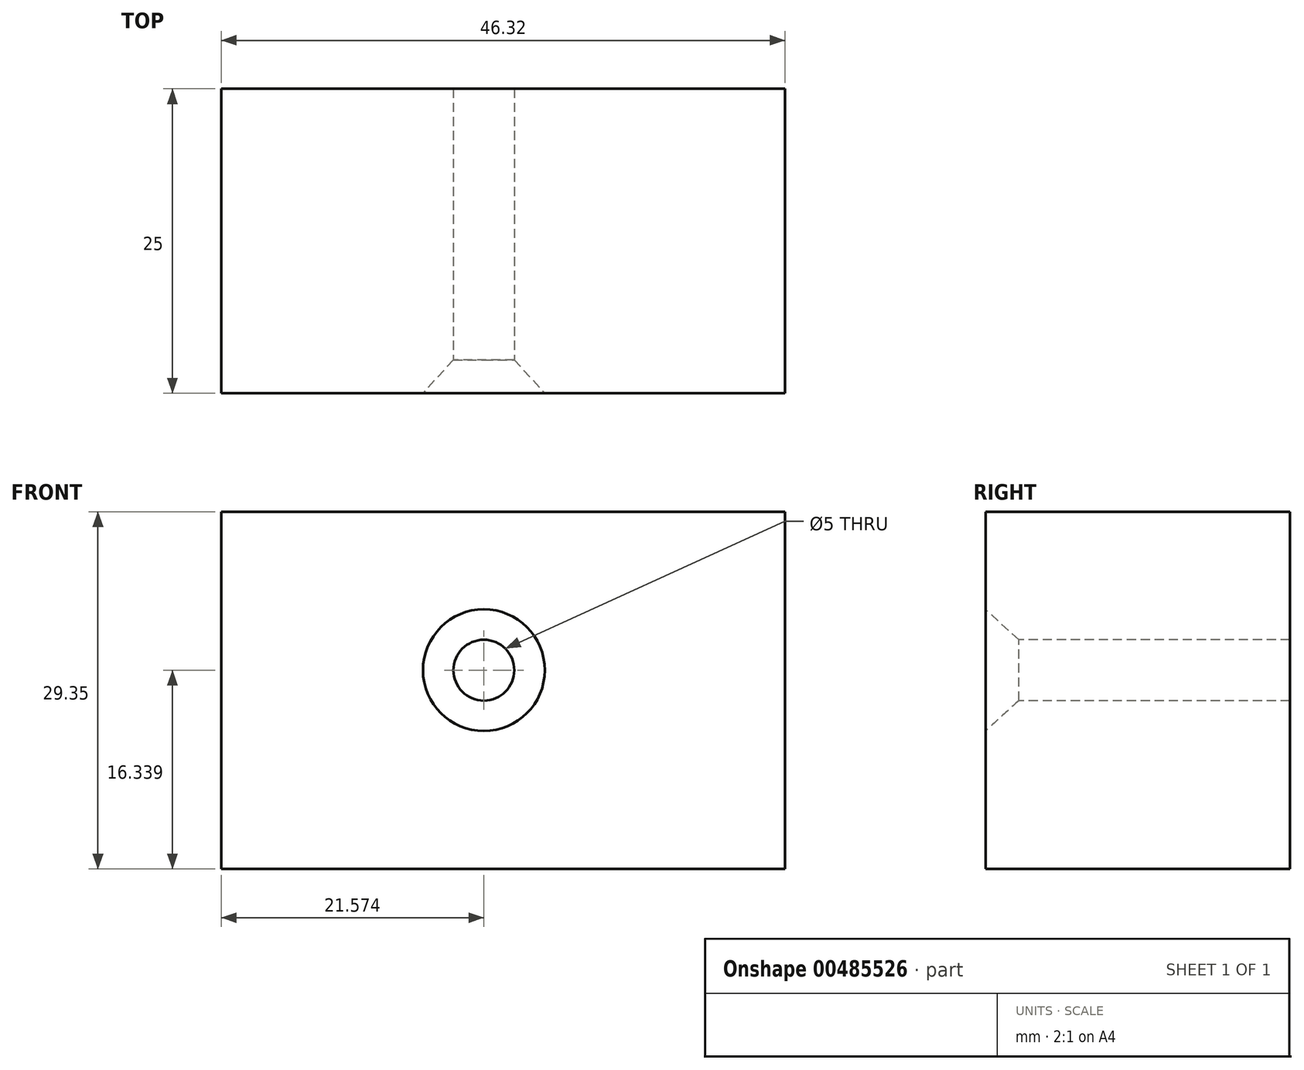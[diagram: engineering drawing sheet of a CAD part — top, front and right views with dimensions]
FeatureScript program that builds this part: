
annotation { "Feature Type Name" : "Feature", "Feature Type Description" : "" }
export const myFeature = defineFeature(function(context is Context, id is Id, definition is map)
    precondition{}
    {
        {
            var Q0;
            Q0=qCreatedBy(makeId("Front.planeOp"),FACE);
            var sketch = newSketch(context, id + "F0", { "sketchPlane" : qUnion([Q0])});
            skLineSegment(sketch, "E0.bottom", {"start": v(0, 0) * mm, "end": v(46.32, 0) * mm});
            skLineSegment(sketch, "E0.top", {"start": v(0, 29.35) * mm, "end": v(46.32, 29.35) * mm});
            skLineSegment(sketch, "E0.left", {"start": v(0, 0) * mm, "end": v(0, 29.35) * mm});
            skLineSegment(sketch, "E0.right", {"start": v(46.32, 0) * mm, "end": v(46.32, 29.35) * mm});
            skSolve(sketch);
        }
        {
            var Q0;
            Q0 = qSketchRegion(id + "F0", true);
            extrude(context, id + "F1", {"entities" : qUnion([Q0]), "depth" : 25 * mm});
        }
        {
            var Q0;
            Q0=makeQuery(id+"F1.opExtrude","CAP_FACE",FACE,{"disambiguationData":[OSD([sQuery(id+"F0.wireOp",EDGE,"E0.bottom"),sQuery(id+"F0.wireOp",EDGE,"E0.top"),sQuery(id+"F0.wireOp",EDGE,"E0.left"),sQuery(id+"F0.wireOp",EDGE,"E0.right")])],"isStart":false});
            var sketch = newSketch(context, id + "F2", { "sketchPlane" : qUnion([Q0])});
            skPoint(sketch, "E1", {"position": v(21.57, 16.34) * mm});
            skSolve(sketch);
        }
        {
            var Q0;
            Q0=sQuery(id+"F2.wireOp",VERTEX,"E1");
            var Q1;
            Q1=makeQuery(id+"F1.opExtrude","SWEPT_BODY",BODY,{"disambiguationData":[OSD([sQuery(id+"F0.wireOp",EDGE,"E0.bottom"),sQuery(id+"F0.wireOp",EDGE,"E0.top"),sQuery(id+"F0.wireOp",EDGE,"E0.left"),sQuery(id+"F0.wireOp",EDGE,"E0.right")])]});
            hole(context, id + "F3", {"style" : HoleStyle.C_SINK, "endStyle" : HoleEndStyle.THROUGH, "holeDiameter" : 5 * mm, "cSinkDiameter" : 10 * mm, "cSinkAngle" : 85 * degree, "isTappedThrough" : true, "tappedDepth" : 12 * mm, "tapClearance" : 3, "locations" : qUnion([Q0]), "scope" : qUnion([Q1])});
        }
    });
